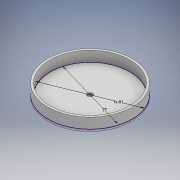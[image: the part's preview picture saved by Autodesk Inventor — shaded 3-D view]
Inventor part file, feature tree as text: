
AUTODESK INVENTOR PART (.ipt)
format: ipt  version: 2017 (Build 210142000, 142)  size: 111,616 bytes
history: native  units: mm
features: extrude x3, sketch x2
ambient origin geometry x8: Origin, YZ Plane, XZ Plane, XY Plane, X Axis, Y Axis, Z Axis, Center Point
bodies: Solid1 (feature_tree)
feature tree (5):
  sketch  "Sketch1"  dims[d1=81.0mm d3=0.0mm]
  extrude  "Extrusion1"  TaperAngle=0.0deg  [1 undecoded]
  extrude  "Extrusion2"  Depth=10.0mm TaperAngle=0.0deg
  extrude  "Extrusion3"  [1 undecoded]
  sketch  "Sketch2"  dims[d5=0.0mm d7=10.0mm d8=0.0mm]
note: 2 required parameter values undecoded (feature->parameter linkage not recoverable at this tier; creation-order binding heuristic only, values carry confidence <= 0.55)
